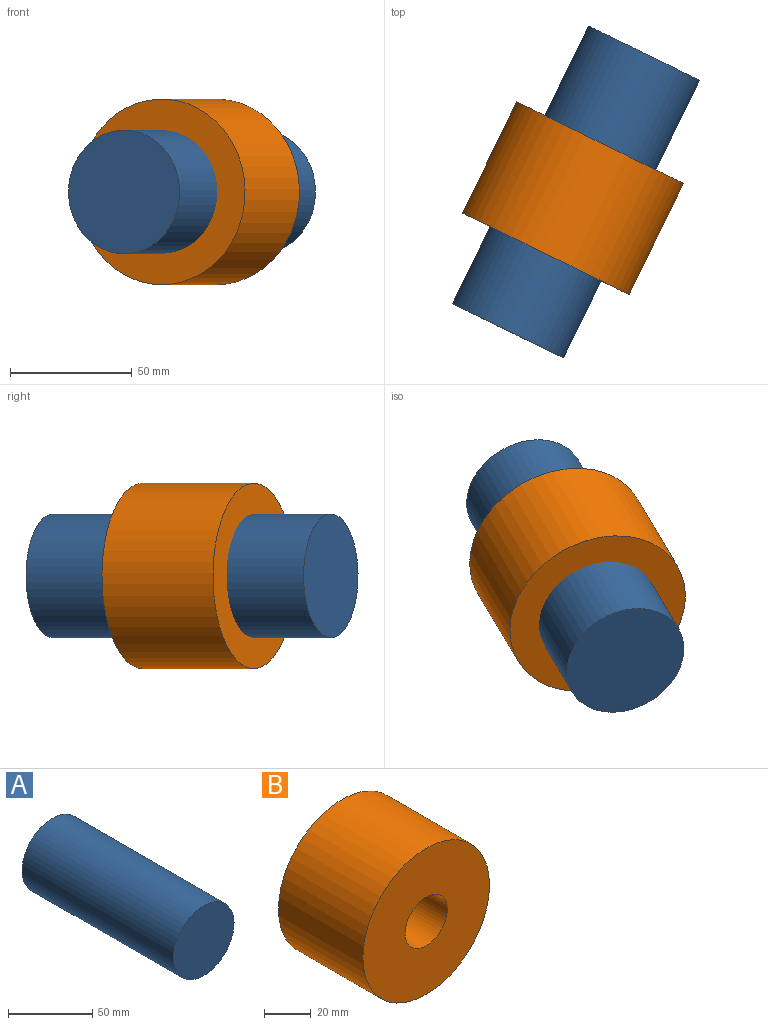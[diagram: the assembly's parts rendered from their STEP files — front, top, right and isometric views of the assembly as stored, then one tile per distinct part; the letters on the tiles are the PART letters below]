
ASSEMBLY  parts=2 mates=1
PART A: 3 faces, bbox 50.8x127x50.8 mm
  f0: cylinder r=25.4mm len=127mm, axis (0,1,0), area 20268.3mm2, adj f1,f2
  f1: plane 50.8x50.8mm, normal (0,-1,0), area 2026.8mm2, adj f0
  f2: plane 50.8x50.8mm, normal (0,1,0), area 2026.8mm2, adj f0
PART B: 4 faces, bbox 76.2x50.8x76.2 mm
  f0: cylinder r=12.7mm len=50.8mm, axis (0,1,0), area 4053.7mm2, adj f2,f3
  f1: cylinder r=38.1mm len=76.2mm, axis (0,1,0), area 12161mm2, adj f2,f3
  f2: plane 76.2x76.2mm, normal (0,-1,0), area 4053.7mm2, adj f0,f1
  f3: plane 76.2x76.2mm, normal (0,1,0), area 4053.7mm2, adj f0,f1
PLACE A rot(axis=(0,-0.01,-1),26.1deg) t=(19.4,22.3,-35.57)mm
PLACE B rot(axis=(0,0,-1),26.1deg) t=(1.4,-14.49,-35.57)mm fixed
MATE cylindrical A.f0 <-> B.f1  axis (0.44,0.9,0) through (-8.51,-34.73,-35.57)mm
